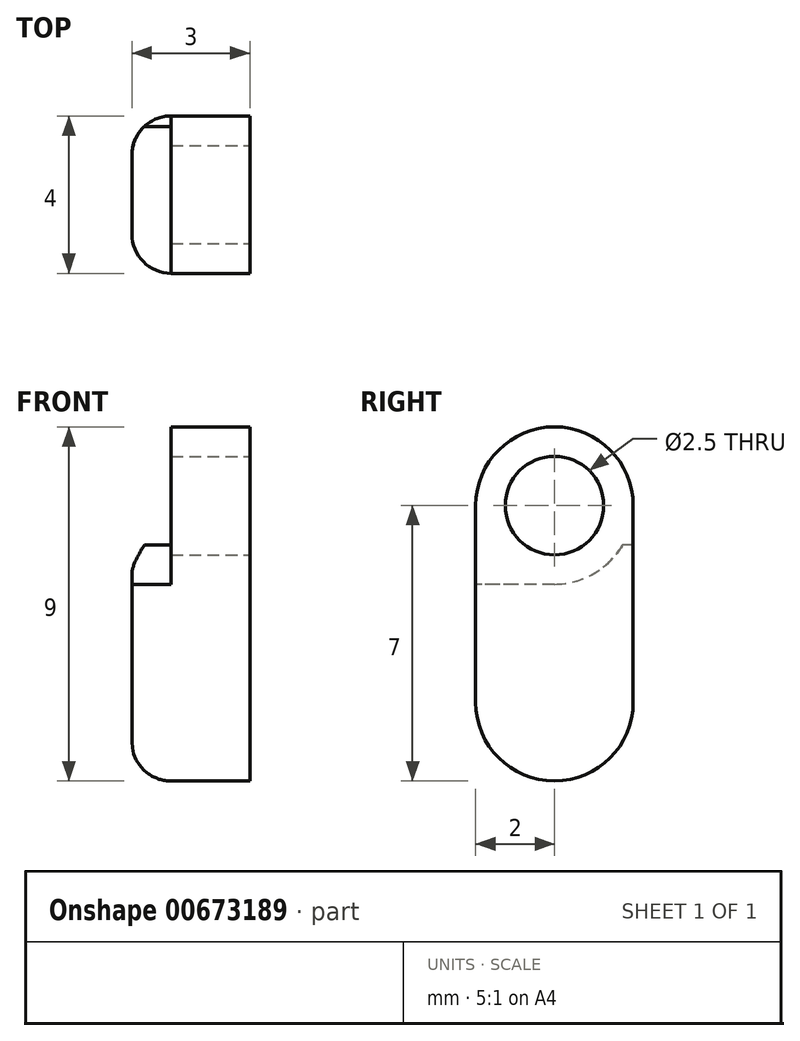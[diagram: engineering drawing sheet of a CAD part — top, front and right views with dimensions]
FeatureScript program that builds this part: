
annotation { "Feature Type Name" : "Feature", "Feature Type Description" : "" }
export const myFeature = defineFeature(function(context is Context, id is Id, definition is map)
    precondition{}
    {
        {
            var Q0;
            Q0=qCreatedBy(makeId("Right.planeOp"),FACE);
            var sketch = newSketch(context, id + "F0", { "sketchPlane" : qUnion([Q0])});
            skCircle(sketch, "E0", {"center": v(0, 0) * mm, "radius": 2 * mm});
            skCircle(sketch, "E1", {"center": v(0, 0) * mm, "radius": 1.25 * mm});
            skLineSegment(sketch, "E2", {"start": v(2, 0) * mm, "end": v(2, -5) * mm});
            skLineSegment(sketch, "E3", {"start": v(2, -5) * mm, "end": v(-2, -5) * mm});
            skLineSegment(sketch, "E4", {"start": v(-2, -5) * mm, "end": v(-2, 0) * mm});
            skCircle(sketch, "E5", {"center": v(0, -5) * mm, "radius": 2 * mm});
            skSolve(sketch);
        }
        {
            var Q0;
            Q0=qSketchRegion(id+"F0",true);
            extrude(context, id + "F1", {"entities" : qUnion([Q0]), "oppositeDirection" : true, "depth" : 2 * mm});
        }
        {
            var Q0;
            Q0=makeQuery(id+"F1.opExtrude","CAP_FACE",FACE,{"disambiguationData":[OSD([sQuery(id+"F0.wireOp",EDGE,"E0"),sQuery(id+"F0.wireOp",EDGE,"E1"),sQuery(id+"F0.wireOp",EDGE,"E2"),sQuery(id+"F0.wireOp",EDGE,"E4"),sQuery(id+"F0.wireOp",EDGE,"E5"),sQuery(id+"F0.wireOp",EDGE,"UKGwOzSf-8W2r-gsbs-ODZy-oFqecLjrtiHH")])],"isStart":false});
            var sketch = newSketch(context, id + "F2", { "sketchPlane" : qUnion([Q0])});
            skArc(sketch, "E6", {"start": v(-1.73, -1) * mm, "mid": v(-1, -1.73) * mm, "end": v(0, -2) * mm});
            skArc(sketch, "E7", {"start": v(0, -3) * mm, "mid": v(-1, -3.27) * mm, "end": v(-1.73, -4) * mm});
            skLineSegment(sketch, "E8", {"start": v(-2, -1) * mm, "end": v(-1.73, -1) * mm});
            skLineSegment(sketch, "E9", {"start": v(0, 0) * mm, "end": v(0, -1.25) * mm, "construction": true});
            skLineSegment(sketch, "E10", {"start": v(2, -2.5) * mm, "end": v(-2, -2.5) * mm, "construction": true});
            skLineSegment(sketch, "E11.MirrorCS", {"start": v(-2, -4) * mm, "end": v(-1.73, -4) * mm});
            skLineSegment(sketch, "E12", {"start": v(0, -2) * mm, "end": v(2, -2) * mm});
            skLineSegment(sketch, "E13", {"start": v(0, -3) * mm, "end": v(2, -3) * mm});
            skPoint(sketch, "E14.MirrorCS.end.orphan", {"position": v(1.73, -4) * mm});
            skPoint(sketch, "E14.MirrorCS.start.orphan", {"position": v(2, -4) * mm});
            skPoint(sketch, "E15.MirrorCS.end.orphan", {"position": v(1.73, -1) * mm});
            skPoint(sketch, "E15.MirrorCS.start.orphan", {"position": v(2, -1) * mm});
            skSolve(sketch);
        }
        {
            var Q0;
            Q0=makeQuery(id+"F2.imprint","IMPRINT",FACE,{"disambiguationData":[TD([[makeQuery(id+"F2.imprint","IMPRINT",EDGE,{"derivedFrom":sQuery(id+"F2.wireOp",EDGE,"E6")}),-1.0]])]});
            var Q1;
            Q1=makeQuery(id+"F2.imprint","IMPRINT",FACE,{"disambiguationData":[TD([[makeQuery(id+"F2.imprint","IMPRINT",EDGE,{"derivedFrom":sQuery(id+"F2.wireOp",EDGE,"E7")}),1.0]])]});
            extrude(context, id + "F3", {"entities" : qUnion([Q0, Q1]), "operationType" : NewBodyOperationType.ADD, "depth" : 1 * mm});
        }
        {
            var Q0;
            Q0=qCreatedBy(makeId("Right.planeOp"),FACE);
            cPlane(context, id + "F4", {"entities" : qUnion([Q0]), "cplaneType" : CPlaneType.OFFSET, "offset" : 1 * mm, "oppositeDirection" : true, "width" : 150 * mm, "height" : 150 * mm});
        }
        {
            var Q0;
            Q0=makeQuery(id+"F7kKs8IQ0HkHr6V_1.1.F3.opExtrude","CAP_EDGE",EDGE,{"disambiguationData":[OSD([sQuery(id+"F0.wireOp",EDGE,"E2")])],"isStart":false});
            var Q1;
            Q1=makeQuery(id+"F3.opExtrude","CAP_EDGE",EDGE,{"disambiguationData":[OSD([sQuery(id+"F0.wireOp",EDGE,"E2")])],"isStart":false});
            var Q2;
            Q2=makeQuery(id+"F7kKs8IQ0HkHr6V_1.1.F3.opExtrude","CAP_EDGE",EDGE,{"disambiguationData":[OSD([sQuery(id+"F0.wireOp",EDGE,"E4")])],"isStart":false});
            var Q3;
            Q3=makeQuery(id+"F3.opExtrude","CAP_EDGE",EDGE,{"disambiguationData":[OSD([sQuery(id+"F0.wireOp",EDGE,"E4")])],"isStart":false});
            fillet(context, id + "F5", {"entities" : qUnion([Q0, Q1, Q2, Q3]), "radius" : 1 * mm, "tangentPropagation" : true, "allowEdgeOverflow" : false});
        }
    });
